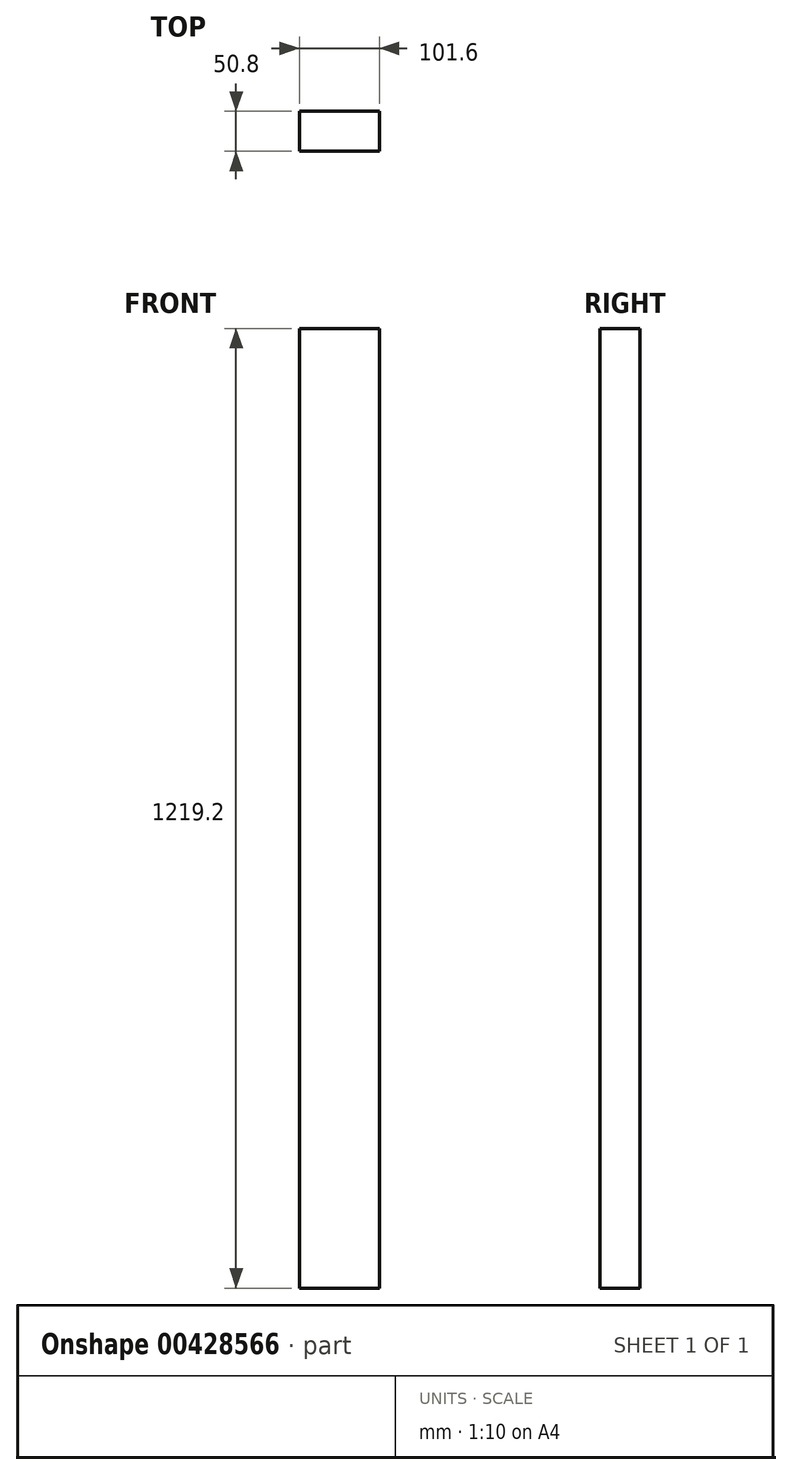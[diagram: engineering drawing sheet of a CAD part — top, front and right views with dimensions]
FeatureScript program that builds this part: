
annotation { "Feature Type Name" : "Feature", "Feature Type Description" : "" }
export const myFeature = defineFeature(function(context is Context, id is Id, definition is map)
    precondition{}
    {
        {
            var Q0;
            Q0=qCreatedBy(makeId("Top.planeOp"),FACE);
            var sketch = newSketch(context, id + "F0", { "sketchPlane" : qUnion([Q0])});
            skLineSegment(sketch, "E0.bottom", {"start": v(0, 0) * mm, "end": v(101.6, 0) * mm});
            skLineSegment(sketch, "E0.top", {"start": v(0, 50.8) * mm, "end": v(101.6, 50.8) * mm});
            skLineSegment(sketch, "E0.left", {"start": v(0, 0) * mm, "end": v(0, 50.8) * mm});
            skLineSegment(sketch, "E0.right", {"start": v(101.6, 0) * mm, "end": v(101.6, 50.8) * mm});
            skSolve(sketch);
        }
        {
            var Q0;
            Q0=makeQuery(id+"F0.imprint","IMPRINT",FACE,{"disambiguationData":[TD([[makeQuery(id+"F0.imprint","IMPRINT",EDGE,{"derivedFrom":sQuery(id+"F0.wireOp",EDGE,"E0.bottom")}),1.0]])]});
            extrude(context, id + "F1", {"entities" : qUnion([Q0]), "depth" : 1219.2 * mm});
        }
    });
